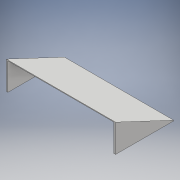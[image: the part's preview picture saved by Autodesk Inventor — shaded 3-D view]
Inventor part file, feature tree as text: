
AUTODESK INVENTOR PART (.ipt)
format: ipt  version: 2018.2 (Build 222227000, 227)  size: 125,440 bytes
history: native  units: mm
features: extrude x4, sketch x4
ambient origin geometry x8: Origin, YZ Plane, XZ Plane, XY Plane, X Axis, Y Axis, Z Axis, Center Point
bodies: Solid1 (feature_tree)
feature tree (8):
  extrude  "Extrusion1"  Depth=160.0mm
  extrude  "Extrusion2"  Depth=82.6mm
  extrude  "Extrusion3"  Depth=155.2mm TaperAngle=0.0deg
  extrude  "Extrusion5"  Depth=2.4mm TaperAngle=0.0deg
  sketch  "Sketch1"  dims[d0=85.0mm d1=160.0mm]
  sketch  "Sketch2"  dims[d2=2.4mm d3=82.6mm]
  sketch  "Sketch3"  dims[d4=155.2mm d5=0.9mm d6=0.0mm]
  sketch  "Sketch5"  dims[d7=40.0mm d8=2.4mm d9=0.0mm d10=2.4mm d11=0.0mm d18=156.0mm d19=0.0mm]
